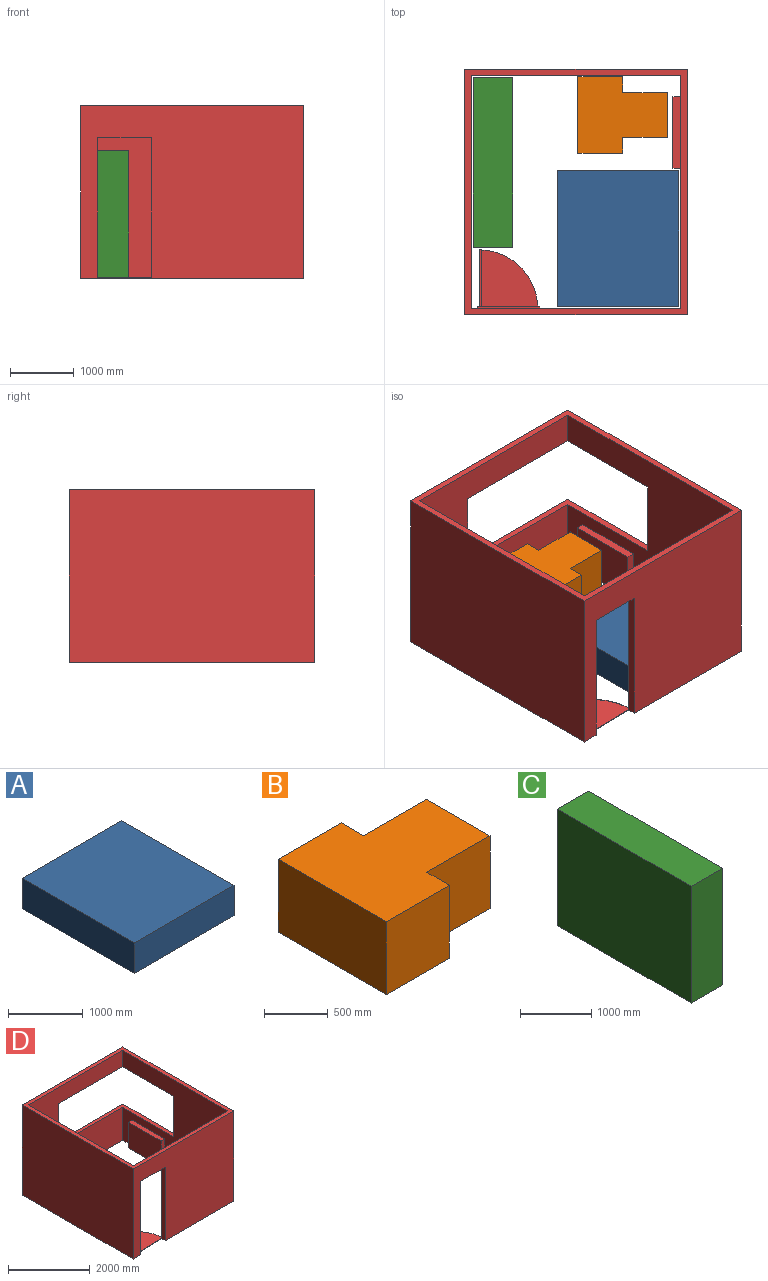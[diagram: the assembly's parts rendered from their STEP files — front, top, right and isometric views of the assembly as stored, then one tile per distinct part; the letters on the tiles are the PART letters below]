
ASSEMBLY  parts=4 mates=3
PART A: 6 faces, bbox 1895x2125x500 mm
  f0: plane 1895x500mm, normal (0,1,0), area 947500mm2, adj f1,f3,f4,f5
  f1: plane 2125x500mm, normal (-1,0,0), area 1062500mm2, adj f0,f2,f4,f5
  f2: plane 1895x500mm, normal (0,-1,0), area 947500mm2, adj f1,f3,f4,f5
  f3: plane 2125x500mm, normal (1,0,0), area 1062500mm2, adj f0,f2,f4,f5
  f4: plane 2125x1895mm, normal (0,0,1), area 4026875mm2, adj f0,f1,f2,f3
  f5: plane 2125x1895mm, normal (0,0,-1), area 4026875mm2, adj f0,f1,f2,f3
PART B: 10 faces, bbox 1400x1200x700 mm
  f0: plane 700x250mm, normal (1,0,0), area 175000mm2, adj f1,f7,f8,f9
  f1: plane 700x700mm, normal (0,-1,0), area 490000mm2, adj f0,f2,f8,f9
  f2: plane 700x700mm, normal (1,0,0), area 490000mm2, adj f1,f3,f8,f9
  f3: plane 700x700mm, normal (0,1,0), area 490000mm2, adj f2,f4,f8,f9
  f4: plane 700x250mm, normal (1,0,0), area 175000mm2, adj f3,f5,f8,f9
  f5: plane 700x700mm, normal (0,1,0), area 490000mm2, adj f4,f6,f8,f9
  f6: plane 1200x700mm, normal (-1,0,0), area 840000mm2, adj f5,f7,f8,f9
  f7: plane 700x700mm, normal (0,-1,0), area 490000mm2, adj f0,f6,f8,f9
  f8: plane 1400x1200mm, normal (0,0,1), area 1330000mm2, adj f0,f1,f2,f3,f4,f5,f6,f7
  f9: plane 1400x1200mm, normal (0,0,-1), area 1330000mm2, adj f0,f1,f2,f3,f4,f5,f6,f7
PART C: 6 faces, bbox 620x2650x2000 mm
  f0: plane 2000x620mm, normal (0,1,0), area 1240000mm2, adj f1,f3,f4,f5
  f1: plane 2650x2000mm, normal (-1,0,0), area 5300000mm2, adj f0,f2,f4,f5
  f2: plane 2000x620mm, normal (0,-1,0), area 1240000mm2, adj f1,f3,f4,f5
  f3: plane 2650x2000mm, normal (1,0,0), area 5300000mm2, adj f0,f2,f4,f5
  f4: plane 2650x620mm, normal (0,0,1), area 1643000mm2, adj f0,f1,f2,f3
  f5: plane 2650x620mm, normal (0,0,-1), area 1643000mm2, adj f0,f1,f2,f3
PART D: 31 faces, bbox 3480x3840x2700 mm
  f0: plane 3840x2700mm, normal (1,0,0), area 8086600mm2, adj f1,f3,f8,f9,f17,f18,f19
  f1: plane 3480x2700mm, normal (0,-1,0), area 7548000mm2, adj f0,f4,f8,f9,f10,f14,f15
  f2: plane 3280x2700mm, normal (0,1,0), area 6658950mm2, adj f5,f7,f8,f9,f11,f12,f13
  f3: plane 3480x2700mm, normal (0,1,0), area 6565600mm2, adj f0,f4,f8,f9,f17,f18,f20
  f4: plane 3840x2700mm, normal (-1,0,0), area 10368000mm2, adj f1,f3,f8,f9
  f5: plane 3640x2700mm, normal (1,0,0), area 9828000mm2, adj f2,f6,f8,f9
  f6: plane 3280x2700mm, normal (0,-1,0), area 6147600mm2, adj f5,f7,f8,f9,f17,f18,f20
  f7: plane 3640x2700mm, normal (-1,0,0), area 6806200mm2, adj f2,f6,f8,f9,f17,f18,f19,f21
  f8: plane 3840x3480mm, normal (0,0,1), area 1424000mm2, adj f0,f1,f2,f3,f4,f5,f6,f7
  f9: plane 3840x3480mm, normal (0,0,-1), area 2131814.3mm2, adj f0,f1,f2,f3,f4,f5,f6,f7
  f10: plane 2200x1015mm, normal (1,0,0), area 2223850mm2, adj f1,f9,f15,f25,f27,f28,f29
  f11: plane 2265x20mm, normal (-1,0,0), area 45300mm2, adj f2,f9,f12,f16
  f12: plane 970x20mm, normal (0,0,1), area 19400mm2, adj f2,f11,f13,f16
  f13: plane 2265x20mm, normal (1,0,0), area 45300mm2, adj f2,f9,f12,f16
  f14: plane 2200x120mm, normal (-1,0,0), area 263991.9mm2, adj f1,f9,f15,f16,f28,f29
  f15: plane 840x120mm, normal (0,0,-1), area 100800mm2, adj f1,f10,f14,f16
  f16: plane 2265x970mm, normal (0,1,0), area 260693.4mm2, adj f9,f11,f12,f13,f14,f15,f26,f27
  f17: plane 2320x1870mm, normal (0,0,-1), area 409000mm2, adj f0,f3,f6,f7,f19,f20
  f18: plane 2320x1870mm, normal (0,0,1), area 409000mm2, adj f0,f3,f6,f7,f19,f20
  f19: plane 1220x100mm, normal (0,1,0), area 122000mm2, adj f0,f7,f17,f18
  f20: plane 1220x100mm, normal (1,0,0), area 122000mm2, adj f3,f6,f17,f18
  f21: plane 1120x125mm, normal (0,0,1), area 140000mm2, adj f7,f22,f23,f24
  f22: plane 770x125mm, normal (0,1,0), area 96250mm2, adj f7,f9,f21,f24
  f23: plane 770x125mm, normal (0,-1,0), area 96250mm2, adj f7,f9,f21,f24
  f24: plane 1120x770mm, normal (-1,0,0), area 862400mm2, adj f9,f21,f22,f23
  f25: plane 2200x40mm, normal (0,1,0), area 88000mm2, adj f9,f10,f26,f27,f30
  f26: plane 2200x895mm, normal (-1,0,0), area 1969000mm2, adj f9,f16,f25,f27
  f27: plane 895x40mm, normal (0,0,1), area 35800mm2, adj f10,f16,f25,f26
  f28: plane 840x19.19mm, normal (0.02,-1,0), area 8402.2mm2, adj f9,f10,f14,f29
  f29: plane 915x875.66mm, normal (0,0,1), area 613414.3mm2, adj f10,f14,f16,f28,f30
  f30: cylinder r=915.87mm len=895mm, axis (0,0,-1), area 13786.4mm2, adj f9,f16,f25,f29
PLACE A t=(48.72,-1279.97,982.77)mm
PLACE B rot(axis=(0,0,-1),0deg) t=(-380.79,-1673.74,982.77)mm
PLACE C t=(39.27,-1274.39,982.77)mm
PLACE D t=(29.22,-1260.89,982.77)mm
MATE planar A.f5 <-> D.f9  axis (0,0,-1) through (-948.78,-167.47,982.77)mm
MATE planar B.f9 <-> D.f9  axis (0,0,-1) through (-972.9,1766.26,982.77)mm
MATE planar C.f5 <-> D.f9  axis (0,0,-1) through (-2910.73,1020.61,982.77)mm
